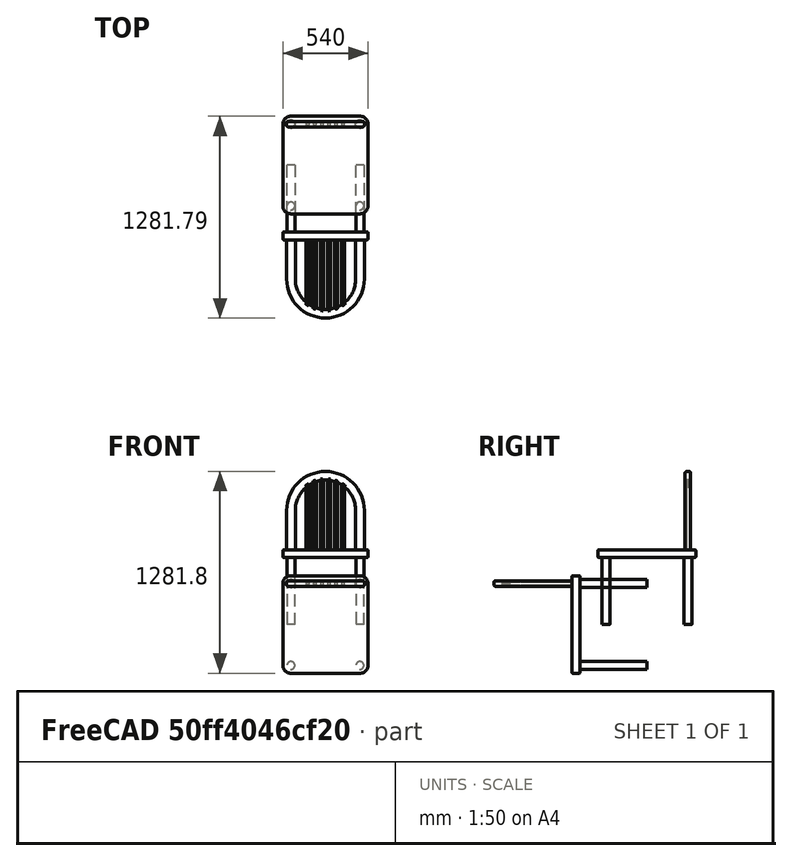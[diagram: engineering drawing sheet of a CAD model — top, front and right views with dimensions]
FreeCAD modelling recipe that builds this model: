
FCSTD DOCUMENT  (FreeCAD 1.0R39109 (Git))
Label: chair01
License: All rights reserved
LicenseURL: https://en.wikipedia.org/wiki/All_rights_reserved
objects: TechDraw::DrawViewDimension×38, Sketcher::SketchObject×8, PartDesign::Pad×8, TechDraw::DrawViewBalloon×7, TechDraw::DrawViewAnnotation×7, PartDesign::Body×6, TechDraw::DrawProjGroupItem×6, TechDraw::DrawSVGTemplate×5, TechDraw::DrawPage×5, PartDesign::SubShapeBinder×4, App::Part×3, PartDesign::Fillet×3, TechDraw::DrawViewSection×2, TechDraw::DrawViewDetail×1, TechDraw::DrawProjGroup×1, Part::FeaturePython×1
note: 130 computed .brp shape members not serialized (recipe doc carries the construction recipe); baked Part::Feature solids carry a one-line shape summary decoded from their .brp

FEATURE [Sketcher::SketchObject] Sketch
  ArcFitTolerance = 1e-06
  AttachmentSupport = -> [XZ_Plane]
  FullyConstrained = true
  MakeInternals = false
  MapMode = 5
  Placement = pos=(0,0,0) rot=(1,0,0;1.5708rad)
  sketch-geometry (6):
    g0: LineSegment [constr] StartX=-219 StartY=-260 StartZ=0 EndX=219 EndY=-260 EndZ=0
    g1: LineSegment [constr] StartX=219 StartY=-260 StartZ=0 EndX=219 EndY=260 EndZ=0
    g2: LineSegment [constr] StartX=219 StartY=260 StartZ=0 EndX=-219 EndY=260 EndZ=0
    g3: LineSegment [constr] StartX=-219 StartY=260 StartZ=0 EndX=-219 EndY=-260 EndZ=0
    g4: GeomPoint [constr] X=0 Y=0 Z=0
    g5: Circle CenterX=219 CenterY=-260 CenterZ=0 NormalX=0 NormalY=0 NormalZ=1 AngleXU=0 Radius=25
  constraints (14):
    c: Coincident(g0,g1)
    c: Coincident(g1,g2)
    c: Coincident(g2,g3)
    c: Coincident(g3,g0)
    c: Horizontal(g0)
    c: Horizontal(g2)
    c: Vertical(g1)
    c: Vertical(g3)
    c: Symmetric(g2,g0,g4)
    c: Distance(g1,g3) = 438
    c: Distance(g0,g2) = 520
    c: Coincident(g4,g-1)
    c: Diameter(g5) = 50
    c: Coincident(g5,g0)
FEATURE [PartDesign::Pad] Pad
  Direction = (0,-1,2e-16)
  Length = 425
  Length2 = 10
  Placement = pos=(0,0,0) rot=(1,0,0;1.5708rad)
  Profile = -> Sketch
  ReferenceAxis = -> Sketch [N_Axis]
  Refine = true
  Suppressed = false
  Type = 0
FEATURE [PartDesign::Body] Body  label="foot1"
  AllowCompound = false
  Group = -> [Sketch,Pad]
  Origin = -> Origin
  Tip = -> Pad
FEATURE [PartDesign::SubShapeBinder] Binder
  BindCopyOnChange = 0
  BindMode = 0
  ClaimChildren = false
  Context = -> Part001 [Body001.Binder.]
  Fuse = false
  MakeFace = true
  OffsetFill = false
  OffsetIntersection = false
  OffsetJoinType = 0
  OffsetOpenResult = false
  PartialLoad = false
  Refine = true
  Relative = true
  Support = -> [Pad[Face3]]
  _Version = 2
FEATURE [Sketcher::SketchObject] Sketch001
  ArcFitTolerance = 1e-06
  AttachmentSupport = -> [Binder]
  ExternalGeometry = -> [Binder]
  FullyConstrained = true
  MakeInternals = false
  MapMode = 5
  Placement = pos=(0,-425,0) rot=(1,0,0;1.5708rad)
  sketch-geometry (5):
    g0: LineSegment StartX=-270 StartY=310 StartZ=0 EndX=-270 EndY=-310 EndZ=0
    g1: LineSegment StartX=-270 StartY=-310 StartZ=0 EndX=270 EndY=-310 EndZ=0
    g2: LineSegment StartX=270 StartY=-310 StartZ=0 EndX=270 EndY=310 EndZ=0
    g3: LineSegment StartX=270 StartY=310 StartZ=0 EndX=-270 EndY=310 EndZ=0
    g4: GeomPoint [constr] X=0 Y=0 Z=0
  constraints (12):
    c: Coincident(g0,g1)
    c: Coincident(g1,g2)
    c: Coincident(g2,g3)
    c: Coincident(g3,g0)
    c: Vertical(g0)
    c: Vertical(g2)
    c: Horizontal(g1)
    c: Horizontal(g3)
    c: Symmetric(g2,g0,g4)
    c: Coincident(g4,g-1)
    c: DistanceX(g1,g1) = 540
    c: DistanceY(g2,g2) = 620
FEATURE [PartDesign::Pad] Pad001
  Direction = (0,-1,2e-16)
  Length = 50
  Length2 = 10
  Profile = -> Sketch001
  ReferenceAxis = -> Sketch001 [N_Axis]
  Refine = true
  Suppressed = false
  Type = 0
FEATURE [Sketcher::SketchObject] Sketch002
  ArcFitTolerance = 1e-06
  AttachmentSupport = -> [XZ_Plane002]
  FullyConstrained = true
  MakeInternals = false
  MapMode = 5
  Placement = pos=(0,0,0) rot=(1,0,0;1.5708rad)
  sketch-geometry (6):
    g0: LineSegment [constr] StartX=-219 StartY=-260 StartZ=0 EndX=219 EndY=-260 EndZ=0
    g1: LineSegment [constr] StartX=219 StartY=-260 StartZ=0 EndX=219 EndY=260 EndZ=0
    g2: LineSegment [constr] StartX=219 StartY=260 StartZ=0 EndX=-219 EndY=260 EndZ=0
    g3: LineSegment [constr] StartX=-219 StartY=260 StartZ=0 EndX=-219 EndY=-260 EndZ=0
    g4: GeomPoint [constr] X=0 Y=0 Z=0
    g5: Circle CenterX=219 CenterY=260 CenterZ=0 NormalX=0 NormalY=0 NormalZ=1 AngleXU=0 Radius=25
  constraints (14):
    c: Coincident(g0,g1)
    c: Coincident(g1,g2)
    c: Coincident(g2,g3)
    c: Coincident(g3,g0)
    c: Horizontal(g0)
    c: Horizontal(g2)
    c: Vertical(g1)
    c: Vertical(g3)
    c: Symmetric(g2,g0,g4)
    c: Distance(g1,g3) = 438
    c: Distance(g0,g2) = 520
    c: Coincident(g4,g-1)
    c: Coincident(g5,g1)
    c: Diameter(g5) = 50
FEATURE [PartDesign::Pad] Pad002
  Direction = (0,-1,2e-16)
  Length = 425
  Length2 = 10
  Placement = pos=(0,0,0) rot=(1,0,0;1.5708rad)
  Profile = -> Sketch002
  ReferenceAxis = -> Sketch002 [N_Axis]
  Refine = true
  Suppressed = false
  Type = 0
FEATURE [PartDesign::Body] Body002  label="foot2"
  AllowCompound = false
  Group = -> [Sketch002,Pad002]
  Origin = -> Origin002
  Tip = -> Pad002
FEATURE [Sketcher::SketchObject] Sketch003
  ArcFitTolerance = 1e-06
  AttachmentSupport = -> [XZ_Plane003]
  FullyConstrained = true
  MakeInternals = false
  MapMode = 5
  Placement = pos=(0,0,0) rot=(1,0,0;1.5708rad)
  sketch-geometry (6):
    g0: LineSegment [constr] StartX=-219 StartY=-260 StartZ=0 EndX=219 EndY=-260 EndZ=0
    g1: LineSegment [constr] StartX=219 StartY=-260 StartZ=0 EndX=219 EndY=260 EndZ=0
    g2: LineSegment [constr] StartX=219 StartY=260 StartZ=0 EndX=-219 EndY=260 EndZ=0
    g3: LineSegment [constr] StartX=-219 StartY=260 StartZ=0 EndX=-219 EndY=-260 EndZ=0
    g4: GeomPoint [constr] X=0 Y=0 Z=0
    g5: Circle CenterX=-219 CenterY=-260 CenterZ=0 NormalX=0 NormalY=0 NormalZ=1 AngleXU=0 Radius=25
  constraints (14):
    c: Coincident(g0,g1)
    c: Coincident(g1,g2)
    c: Coincident(g2,g3)
    c: Coincident(g3,g0)
    c: Horizontal(g0)
    c: Horizontal(g2)
    c: Vertical(g1)
    c: Vertical(g3)
    c: Symmetric(g2,g0,g4)
    c: Distance(g1,g3) = 438
    c: Distance(g0,g2) = 520
    c: Coincident(g4,g-1)
    c: Coincident(g5,g0)
    c: Diameter(g5) = 50
FEATURE [PartDesign::Pad] Pad003
  Direction = (0,-1,2e-16)
  Length = 425
  Length2 = 10
  Placement = pos=(0,0,0) rot=(1,0,0;1.5708rad)
  Profile = -> Sketch003
  ReferenceAxis = -> Sketch003 [N_Axis]
  Refine = true
  Suppressed = false
  Type = 0
FEATURE [PartDesign::Body] Body003  label="foot3"
  AllowCompound = false
  Group = -> [Sketch003,Pad003]
  Origin = -> Origin003
  Tip = -> Pad003
FEATURE [Sketcher::SketchObject] Sketch004
  ArcFitTolerance = 1e-06
  AttachmentSupport = -> [XZ_Plane004]
  FullyConstrained = false
  MakeInternals = false
  MapMode = 5
  Placement = pos=(0,0,0) rot=(1,0,0;1.5708rad)
  sketch-geometry (6):
    g0: LineSegment [constr] StartX=-219 StartY=-260 StartZ=0 EndX=219 EndY=-260 EndZ=0
    g1: LineSegment [constr] StartX=-219 StartY=260 StartZ=0 EndX=-219 EndY=-260 EndZ=0
    g2: GeomPoint [constr] X=0 Y=0 Z=0
    g3: Circle CenterX=-219 CenterY=260 CenterZ=0 NormalX=0 NormalY=0 NormalZ=1 AngleXU=0 Radius=25
    g4: LineSegment [constr] StartX=219 StartY=260 StartZ=0 EndX=219 EndY=-260 EndZ=0
    g5: LineSegment [constr] StartX=-219 StartY=260 StartZ=0 EndX=219 EndY=260 EndZ=0
  constraints (12):
    c: Coincident(g1,g0)
    c: Horizontal(g0)
    c: Vertical(g1)
    c: Symmetric(g4,g0,g2)
    c: Distance(g0,g1) = 520
    c: Coincident(g2,g-1)
    c: Diameter(g3) = 50
    c: Coincident(g4,g0)
    c: Vertical(g4)
    c: Coincident(g5,g3)
    c: Coincident(g5,g4)
    c: Horizontal(g5)
FEATURE [PartDesign::Pad] Pad004
  Direction = (0,-1,2e-16)
  Length = 425
  Length2 = 10
  Placement = pos=(0,0,0) rot=(1,0,0;1.5708rad)
  Profile = -> Sketch004
  ReferenceAxis = -> Sketch004 [N_Axis]
  Refine = true
  Suppressed = false
  Type = 0
FEATURE [PartDesign::Body] Body004  label="foot4"
  AllowCompound = false
  Group = -> [Sketch004,Pad004]
  Origin = -> Origin004
  Tip = -> Pad004
FEATURE [App::Part] Part  label="foot"
  Group = -> [Body004,Body003,Body002,Body]
  Origin = -> Origin005
FEATURE [PartDesign::SubShapeBinder] Binder001
  BindCopyOnChange = 0
  BindMode = 0
  ClaimChildren = false
  Context = -> Part001 [Body005.Binder001.]
  Fuse = false
  MakeFace = true
  OffsetFill = false
  OffsetIntersection = false
  OffsetJoinType = 0
  OffsetOpenResult = false
  PartialLoad = false
  Refine = true
  Relative = true
  Support = -> [Body001]
  _Version = 2
FEATURE [PartDesign::SubShapeBinder] Binder002
  BindCopyOnChange = 0
  BindMode = 0
  ClaimChildren = false
  Context = -> Part001 [Body005.Binder002.]
  Fuse = false
  MakeFace = true
  OffsetFill = false
  OffsetIntersection = false
  OffsetJoinType = 0
  OffsetOpenResult = false
  PartialLoad = false
  Refine = true
  Relative = true
  Support = -> [Part[Body004.]]
  _Version = 2
FEATURE [Sketcher::SketchObject] Sketch005
  ArcFitTolerance = 1e-06
  AttachmentSupport = -> [Binder001]
  ExternalGeometry = -> [Binder002]
  FullyConstrained = true
  MakeInternals = false
  MapMode = 5
  Placement = pos=(0,-475,0) rot=(1,0,0;1.5708rad)
  sketch-geometry (5):
    g0: LineSegment StartX=-246.5 StartY=242.5 StartZ=0 EndX=-191.5 EndY=242.5 EndZ=0
    g1: LineSegment StartX=-191.5 StartY=242.5 StartZ=0 EndX=-191.5 EndY=277.5 EndZ=0
    g2: LineSegment StartX=-191.5 StartY=277.5 StartZ=0 EndX=-246.5 EndY=277.5 EndZ=0
    g3: LineSegment StartX=-246.5 StartY=277.5 StartZ=0 EndX=-246.5 EndY=242.5 EndZ=0
    g4: GeomPoint [constr] X=-219 Y=260 Z=0
  constraints (12):
    c: Coincident(g0,g1)
    c: Coincident(g1,g2)
    c: Coincident(g2,g3)
    c: Coincident(g3,g0)
    c: Horizontal(g0)
    c: Horizontal(g2)
    c: Vertical(g1)
    c: Vertical(g3)
    c: Symmetric(g2,g0,g4)
    c: Coincident(g4,g-3)
    c: DistanceX(g2,g2) = 55
    c: DistanceY(g1,g1) = 35
FEATURE [PartDesign::Pad] Pad005
  Direction = (0,-1,2e-16)
  Length = 250
  Length2 = 10
  Profile = -> Sketch005
  ReferenceAxis = -> Sketch005 [N_Axis]
  Refine = true
  Suppressed = false
  Type = 0
FEATURE [PartDesign::SubShapeBinder] Binder003
  BindCopyOnChange = 0
  BindMode = 0
  ClaimChildren = false
  Context = -> Part001 [Body005.Binder003.]
  Fuse = false
  MakeFace = true
  OffsetFill = false
  OffsetIntersection = false
  OffsetJoinType = 0
  OffsetOpenResult = false
  PartialLoad = false
  Refine = true
  Relative = true
  Support = -> [Part[Body002.]]
  _Version = 2
FEATURE [Sketcher::SketchObject] Sketch006
  ArcFitTolerance = 1e-06
  AttachmentSupport = -> [Pad005]
  ExternalGeometry = -> [Pad005,Binder003]
  FullyConstrained = true
  MakeInternals = false
  MapMode = 5
  Placement = pos=(0,5.34e-14,242.5) rot=(1,0,0;3.14159rad)
  sketch-geometry (6):
    g0: LineSegment StartX=192.09 StartY=475 StartZ=0 EndX=192.09 EndY=725 EndZ=0
    g1: LineSegment StartX=247.09 StartY=475 StartZ=0 EndX=247.09 EndY=725 EndZ=0
    g2: LineSegment StartX=192.09 StartY=475 StartZ=0 EndX=247.09 EndY=475 EndZ=0
    g3: ArcOfCircle CenterX=0.295 CenterY=725 CenterZ=0 NormalX=0 NormalY=0 NormalZ=1 AngleXU=0 Radius=191.795 StartAngle=0 EndAngle=3.14159
    g4: ArcOfCircle CenterX=0.295 CenterY=725 CenterZ=0 NormalX=0 NormalY=0 NormalZ=1 AngleXU=0 Radius=246.795 StartAngle=1e-16 EndAngle=3.14159
    g5: LineSegment StartX=-246.5 StartY=725 StartZ=0 EndX=-191.5 EndY=725 EndZ=0
  constraints (16):
    c: Parallel(g1,g0)
    c: Horizontal(g0,g1)
    c: Horizontal(g1,g-3)
    c: Vertical(g1)
    c: Horizontal(g2)
    c: Coincident(g1,g2)
    c: Coincident(g0,g2)
    c: Coincident(g3,g-3)
    c: Coincident(g4,g-3)
    c: Tangent(g4,g1) = -1.5708
    c: Equal(g2,g-5)
    c: DistanceX(g0) = 192.09
    c: Tangent(g3,g0) = -1.5708
    c: Equal(g-6,g0)
    c: Coincident(g5,g4)
    c: Coincident(g5,g3)
FEATURE [PartDesign::Pad] Pad006
  BaseFeature = -> Pad005
  Direction = (0,0,-1)
  Length = 35
  Length2 = 10
  Profile = -> Sketch006
  ReferenceAxis = -> Sketch006 [N_Axis]
  Refine = true
  Reversed = true
  Suppressed = false
  Type = 0
FEATURE [Sketcher::SketchObject] Sketch007
  ArcFitTolerance = 1e-06
  AttachmentSupport = -> [Binder001]
  ExternalGeometry = -> [Pad006]
  FullyConstrained = true
  MakeInternals = false
  MapMode = 5
  Placement = pos=(0,-475,0) rot=(1,0,0;1.5708rad)
  sketch-geometry (13):
    g0: Circle CenterX=-112.5 CenterY=260 CenterZ=0 NormalX=0 NormalY=0 NormalZ=1 AngleXU=0 Radius=10
    g1: Circle CenterX=-67.5 CenterY=260 CenterZ=0 NormalX=0 NormalY=0 NormalZ=1 AngleXU=0 Radius=10
    g2: Circle CenterX=-22.5 CenterY=260 CenterZ=0 NormalX=0 NormalY=0 NormalZ=1 AngleXU=0 Radius=10
    g3: Circle CenterX=22.5 CenterY=260 CenterZ=0 NormalX=0 NormalY=0 NormalZ=1 AngleXU=0 Radius=10
    g4: Circle CenterX=67.5 CenterY=260 CenterZ=0 NormalX=0 NormalY=0 NormalZ=1 AngleXU=0 Radius=10
    g5: Circle CenterX=112.5 CenterY=260 CenterZ=0 NormalX=0 NormalY=0 NormalZ=1 AngleXU=0 Radius=10
    g6: LineSegment [constr] StartX=-112.5 StartY=260 StartZ=0 EndX=-67.5 EndY=260 EndZ=0
    g7: LineSegment [constr] StartX=-67.5 StartY=260 StartZ=0 EndX=-22.5 EndY=260 EndZ=0
    g8: LineSegment [constr] StartX=-22.5 StartY=260 StartZ=0 EndX=22.5 EndY=260 EndZ=0
    g9: LineSegment [constr] StartX=22.5 StartY=260 StartZ=0 EndX=67.5 EndY=260 EndZ=0
    g10: LineSegment [constr] StartX=67.5 StartY=260 StartZ=0 EndX=112.5 EndY=260 EndZ=0
    g11: LineSegment [constr] StartX=-191.5 StartY=260 StartZ=0 EndX=-112.5 EndY=260 EndZ=0
    g12: LineSegment [constr] StartX=112.5 StartY=260 StartZ=0 EndX=192.09 EndY=260 EndZ=0
  constraints (31):
    c: Coincident(g6,g0)
    c: Coincident(g6,g1)
    c: Horizontal(g6)
    c: Coincident(g7,g1)
    c: Coincident(g7,g2)
    c: Coincident(g8,g2)
    c: Coincident(g8,g3)
    c: Coincident(g9,g3)
    c: Coincident(g9,g4)
    c: Coincident(g10,g4)
    c: Coincident(g10,g5)
    c: Horizontal(g10)
    c: Equal(g6,g7)
    c: Equal(g7,g8)
    c: Equal(g8,g9)
    c: Equal(g9,g10)
    c: Equal(g0,g1)
    c: Equal(g1,g2)
    c: Equal(g2,g3)
    c: Equal(g3,g4)
    c: Equal(g4,g5)
    c: Horizontal(g7)
    c: Horizontal(g9)
    c: Coincident(g11,g0)
    c: Horizontal(g11)
    c: Coincident(g12,g5)
    c: Symmetric(g-4,g-4,g12)
    c: Symmetric(g-3,g-3,g11)
    c: Symmetric(g3,g2,g-2)
    c: Diameter(g0) = 20
    c: DistanceX(g2,g3) = 45
FEATURE [PartDesign::Pad] Pad007
  BaseFeature = -> Pad006
  Direction = (0,-1,2e-16)
  Length = 445
  Length2 = 10
  Profile = -> Sketch007
  ReferenceAxis = -> Sketch007 [N_Axis]
  Refine = true
  Suppressed = false
  Type = 0
FEATURE [PartDesign::Fillet] Fillet
  Base = -> Pad007 [Edge13,Edge19,Edge15,Edge16]
  BaseFeature = -> Pad007
  Radius = 10
  Refine = true
  SupportTransform = false
  Suppressed = false
  UseAllEdges = false
FEATURE [PartDesign::Body] Body005  label="backrest"
  AllowCompound = false
  Group = -> [Binder001,Sketch005,Binder002,Pad005,Sketch006,Binder003,Pad006,Sketch007,Pad007,Fillet]
  Origin = -> Origin006
  Tip = -> Fillet
FEATURE [PartDesign::Fillet] Fillet001
  Base = -> Pad001 [Edge5,Edge2,Edge8,Edge1]
  BaseFeature = -> Pad001
  Radius = 50
  Refine = true
  SupportTransform = false
  Suppressed = false
  UseAllEdges = false
FEATURE [PartDesign::Fillet] Fillet002
  Base = -> Fillet001 [Edge20,Edge8]
  BaseFeature = -> Fillet001
  Radius = 5
  Refine = true
  SupportTransform = false
  Suppressed = false
  UseAllEdges = false
FEATURE [PartDesign::Body] Body001  label="seat_surface"
  AllowCompound = false
  Group = -> [Binder,Sketch001,Pad001,Fillet001,Fillet002]
  Origin = -> Origin001
  Tip = -> Fillet002
FEATURE [App::Part] Part001  label="chair01_p"
  Group = -> [Body001,Part,Body005]
  Origin = -> Origin007
FEATURE [TechDraw::DrawSVGTemplate] Template  label="テンプレート"
  Height = 210
  Orientation = 1
  Template = <userpath>/AppData/Local/Programs/FreeCAD 1.0/data/Mod/TechDraw/Templates/A4_Landscape_blank.svg
  Width = 297
FEATURE [TechDraw::DrawProjGroupItem] View  label="平面図"
  CoarseView = false
  Direction = (0,-1,0)
  Focus = 100
  HardHidden = true
  IsoCount = 0
  IsoHidden = false
  IsoVisible = false
  LockPosition = false
  Perspective = false
  Rotation = 0
  RotationVector = (1,0,0)
  Scale = 0.25
  ScaleType = 2
  ScrubCount = 1
  SeamHidden = false
  SeamVisible = false
  SmoothHidden = false
  SmoothVisible = true
  Source = -> [Part001]
  Type = 0
  X = 141.468
  XDirection = (1,0,0)
  Y = 99.3312
FEATURE [TechDraw::DrawViewDimension] Dimension  label="寸法"
  AngleOverride = false
  Arbitrary = false
  ArbitraryTolerances = false
  BoxCorners = (2) [(-67.5,-77.5,-1e-07),(67.5,77.5,1e-07)]
  EqualTolerance = true
  ExtensionAngle = 0
  FormatSpec = %.2w
  FormatSpecOverTolerance = %+.2w
  FormatSpecUnderTolerance = %+.2w
  Inverted = false
  LineAngle = 0
  LockPosition = false
  MeasureType = 1
  OverTolerance = 0
  References2D = -> [View]
  Rotation = 0
  Scale = 0.2
  ScaleType = 2
  TheoreticalExact = false
  Type = 2
  UnderTolerance = 0
  X = 93.6885
  Y = 0
FEATURE [TechDraw::DrawViewDimension] Dimension001  label="寸法001"
  AngleOverride = false
  Arbitrary = false
  ArbitraryTolerances = false
  BoxCorners = (2) [(-67.5,-77.5,-1e-07),(67.5,77.5,1e-07)]
  EqualTolerance = true
  ExtensionAngle = 0
  FormatSpec = %.2w
  FormatSpecOverTolerance = %+.2w
  FormatSpecUnderTolerance = %+.2w
  Inverted = false
  LineAngle = 0
  LockPosition = false
  MeasureType = 1
  OverTolerance = 0
  References2D = -> [View]
  Rotation = 0
  Scale = 0.2
  ScaleType = 2
  TheoreticalExact = false
  Type = 2
  UnderTolerance = 0
  X = 76.7116
  Y = 0
FEATURE [TechDraw::DrawViewDimension] Dimension003  label="寸法003"
  AngleOverride = false
  Arbitrary = false
  ArbitraryTolerances = false
  BoxCorners = (2) [(-67.5,-77.5,-1e-07),(67.5,77.5,1e-07)]
  EqualTolerance = true
  ExtensionAngle = 0
  FormatSpec = %.2w
  FormatSpecOverTolerance = %+.2w
  FormatSpecUnderTolerance = %+.2w
  Inverted = false
  LineAngle = 0
  LockPosition = false
  MeasureType = 1
  OverTolerance = 0
  References2D = -> [View]
  Rotation = 0
  Scale = 0.2
  ScaleType = 2
  TheoreticalExact = false
  Type = 1
  UnderTolerance = 0
  X = 0
  Y = 106.033
FEATURE [TechDraw::DrawViewBalloon] Balloon  label="吹き出し"
  BubbleShape = 1
  EndType = 0
  EndTypeScale = 1
  KinkLength = 5
  LockPosition = false
  OriginX = 255.355
  OriginY = 295.355
  Rotation = 0
  Scale = 0.2
  ScaleType = 2
  ShapeScale = 1
  SourceView = -> View
  Text = R50
  TextWrapLen = -1
  X = 443.839
  Y = 387.538
FEATURE [TechDraw::DrawSVGTemplate] Template001  label="テンプレート001"
  Height = 210
  Orientation = 1
  Template = <userpath>/AppData/Local/Programs/FreeCAD 1.0/data/Mod/TechDraw/Templates/A4_Landscape_blank.svg
  Width = 297
FEATURE [TechDraw::DrawProjGroupItem] View001  label="正面図"
  CoarseView = false
  Direction = (0,0,-1)
  Focus = 100
  HardHidden = true
  IsoCount = 0
  IsoHidden = false
  IsoVisible = false
  LockPosition = false
  Perspective = false
  Rotation = 0
  RotationVector = (1,0,0)
  Scale = 0.2
  ScaleType = 2
  ScrubCount = 1
  SeamHidden = false
  SeamVisible = false
  SmoothHidden = false
  SmoothVisible = true
  Source = -> [Part001]
  Type = 0
  X = 64.7665
  XDirection = (1,0,0)
  Y = 110.024
FEATURE [TechDraw::DrawViewDimension] Dimension004  label="寸法004"
  AngleOverride = false
  Arbitrary = false
  ArbitraryTolerances = false
  BoxCorners = (2) [(-54,-97.1795,-1e-07),(54,97.1795,1e-07)]
  EqualTolerance = true
  ExtensionAngle = 0
  FormatSpec = %.2w
  FormatSpecOverTolerance = %+.2w
  FormatSpecUnderTolerance = %+.2w
  Inverted = false
  LineAngle = 0
  LockPosition = false
  MeasureType = 1
  OverTolerance = 0
  References2D = -> [View001]
  Rotation = 0
  Scale = 0.2
  ScaleType = 2
  TheoreticalExact = false
  Type = 2
  UnderTolerance = 0
  X = 82.1171
  Y = -54.6795
FEATURE [TechDraw::DrawViewDetail] Detail  label="Detail 詳細①"
  AnchorPoint = (266.87,-34.91,0)
  BaseView = -> View001
  CoarseView = false
  Direction = (0,0,-1)
  Focus = 100
  HardHidden = true
  IsoCount = 0
  IsoHidden = false
  IsoVisible = false
  LockPosition = false
  Perspective = false
  Radius = 30
  Reference = 詳細①
  Rotation = 0
  Scale = 1.2
  ScaleType = 2
  ScrubCount = 1
  SeamHidden = false
  SeamVisible = false
  ShowHighlight = true
  ShowMatting = true
  SmoothHidden = false
  SmoothVisible = true
  Source = -> [Part001]
  X = 216.677
  XDirection = (1,0,0)
  Y = 98.1897
FEATURE [TechDraw::DrawViewDimension] Dimension005  label="寸法005"
  AngleOverride = false
  Arbitrary = false
  ArbitraryTolerances = false
  BoxCorners = (2) [(-54,-97.1795,-1e-07),(54,97.1795,1e-07)]
  EqualTolerance = true
  ExtensionAngle = 0
  FormatSpec = R%.2w
  FormatSpecOverTolerance = %+.2w
  FormatSpecUnderTolerance = %+.2w
  Inverted = false
  LineAngle = 0
  LockPosition = false
  MeasureType = 1
  OverTolerance = 0
  References2D = -> [View001]
  Rotation = 0
  Scale = 0.2
  ScaleType = 2
  TheoreticalExact = false
  Type = 4
  UnderTolerance = 0
  X = 58.3026
  Y = 84.7593
FEATURE [TechDraw::DrawViewDimension] Dimension006  label="寸法006"
  AngleOverride = false
  Arbitrary = false
  ArbitraryTolerances = false
  BoxCorners = (2) [(-54,-97.1795,-1e-07),(54,97.1795,1e-07)]
  EqualTolerance = true
  ExtensionAngle = 0
  FormatSpec = %.2w
  FormatSpecOverTolerance = %+.2w
  FormatSpecUnderTolerance = %+.2w
  Inverted = false
  LineAngle = 0
  LockPosition = false
  MeasureType = 1
  OverTolerance = 0
  References2D = -> [View001]
  Rotation = 0
  Scale = 0.2
  ScaleType = 2
  TheoreticalExact = false
  Type = 2
  UnderTolerance = 0
  X = 84.137
  Y = 22.8205
FEATURE [TechDraw::DrawViewBalloon] Balloon001  label="吹き出し001"
  BubbleShape = 1
  EndType = 0
  EndTypeScale = 1
  KinkLength = 5
  LockPosition = false
  OriginX = 1.73973
  OriginY = 22.4786
  Rotation = 0
  Scale = 0.2
  ScaleType = 2
  ShapeScale = 1
  SourceView = -> Detail
  Text = R5
  TextWrapLen = -1
  X = 24.0571
  Y = 26.1222
FEATURE [TechDraw::DrawViewBalloon] Balloon002  label="吹き出し002"
  BubbleShape = 1
  EndType = 0
  EndTypeScale = 1
  KinkLength = 5
  LockPosition = false
  OriginX = 1.6677
  OriginY = -24.5252
  Rotation = 0
  Scale = 0.2
  ScaleType = 2
  ShapeScale = 1
  SourceView = -> Detail
  Text = R5
  TextWrapLen = -1
  X = 25.0104
  Y = -33.4181
FEATURE [TechDraw::DrawViewDimension] Dimension007  label="寸法007"
  AngleOverride = false
  Arbitrary = false
  ArbitraryTolerances = false
  BoxCorners = (2) [(-36.36,-28.8124,-1e-07),(3.75859,31.1876,1e-07)]
  EqualTolerance = true
  ExtensionAngle = 0
  FormatSpec = %.2w
  FormatSpecOverTolerance = %+.2w
  FormatSpecUnderTolerance = %+.2w
  Inverted = false
  LineAngle = 0
  LockPosition = false
  MeasureType = 1
  OverTolerance = 0
  References2D = -> [Detail]
  Rotation = 0
  Scale = 0.2
  ScaleType = 2
  TheoreticalExact = false
  Type = 2
  UnderTolerance = 0
  X = 11.0343
  Y = -1.18759
FEATURE [TechDraw::DrawViewDimension] Dimension008  label="寸法008"
  AngleOverride = false
  Arbitrary = false
  ArbitraryTolerances = false
  BoxCorners = (2) [(-54,-97.1795,-1e-07),(54,97.1795,1e-07)]
  EqualTolerance = true
  ExtensionAngle = 0
  FormatSpec = %.2w
  FormatSpecOverTolerance = %+.2w
  FormatSpecUnderTolerance = %+.2w
  Inverted = false
  LineAngle = 0
  LockPosition = false
  MeasureType = 1
  OverTolerance = 0
  References2D = -> [View001]
  Rotation = 0
  Scale = 0.2
  ScaleType = 2
  TheoreticalExact = false
  Type = 1
  UnderTolerance = 0
  X = 0
  Y = -39.2219
FEATURE [TechDraw::DrawViewDimension] Dimension009  label="寸法009"
  AngleOverride = false
  Arbitrary = false
  ArbitraryTolerances = false
  BoxCorners = (2) [(-54,-97.1795,-1e-07),(54,97.1795,1e-07)]
  EqualTolerance = true
  ExtensionAngle = 0
  FormatSpec = %.2w
  FormatSpecOverTolerance = %+.2w
  FormatSpecUnderTolerance = %+.2w
  Inverted = false
  LineAngle = 0
  LockPosition = false
  MeasureType = 1
  OverTolerance = 0
  References2D = -> [View001]
  Rotation = 0
  Scale = 0.2
  ScaleType = 2
  TheoreticalExact = false
  Type = 1
  UnderTolerance = 0
  X = 43.8
  Y = -102.091
FEATURE [TechDraw::DrawSVGTemplate] Template002  label="テンプレート002"
  Height = 210
  Orientation = 1
  Template = <userpath>/AppData/Local/Programs/FreeCAD 1.0/data/Mod/TechDraw/Templates/A4_Landscape_blank.svg
  Width = 297
FEATURE [TechDraw::DrawProjGroupItem] View002
  CoarseView = false
  Direction = (0,0,-1)
  Focus = 100
  HardHidden = true
  IsoCount = 0
  IsoHidden = false
  IsoVisible = false
  LockPosition = false
  Perspective = false
  Rotation = 0
  RotationVector = (1,0,0)
  Scale = 0.2
  ScaleType = 2
  ScrubCount = 1
  SeamHidden = false
  SeamVisible = false
  SmoothHidden = false
  SmoothVisible = true
  Source = -> [Part001]
  Type = 0
  X = 71.4869
  XDirection = (1,0,0)
  Y = 108.277
FEATURE [TechDraw::DrawViewSection] SectionView  label="セクション  - "
  BaseView = -> View002
  CoarseView = false
  CutSurfaceDisplay = 2
  Direction = (1e-16,1,0)
  FileGeomPattern = <userpath>\AppData\Local\Programs\FreeCAD 1.0\data\Mod/TechDraw/PAT/FCPAT.pat
  FileHatchPattern = <userpath>\AppData\Local\Programs\FreeCAD 1.0\data\Mod/TechDraw/Patterns/simple.svg
  Focus = 100
  FuseBeforeCut = false
  HardHidden = true
  HatchOffset = (0,0,0)
  HatchRotation = 0
  HatchScale = 1
  IsoCount = 0
  IsoHidden = false
  IsoVisible = false
  LockPosition = false
  NameGeomPattern = Diamond
  Perspective = false
  Rotation = 0
  Scale = 0.2
  ScaleType = 2
  ScrubCount = 1
  SeamHidden = false
  SeamVisible = false
  SectionDirection = 4
  SectionLineStretch = 1
  SectionNormal = (1e-16,1,0)
  SectionOrigin = (0,-579.9,0)
  SmoothHidden = false
  SmoothVisible = true
  Source = -> [Part001]
  TrimAfterCut = false
  UsePreviousCut = false
  X = 220.723
  XDirection = (1,-1e-16,0)
  Y = 183.206
FEATURE [TechDraw::DrawViewSection] SectionView001  label="セクション001  - "
  BaseView = -> View002
  CoarseView = false
  CutSurfaceDisplay = 2
  Direction = (1e-16,-1,0)
  FileGeomPattern = <userpath>\AppData\Local\Programs\FreeCAD 1.0\data\Mod/TechDraw/PAT/FCPAT.pat
  FileHatchPattern = <userpath>\AppData\Local\Programs\FreeCAD 1.0\data\Mod/TechDraw/Patterns/simple.svg
  Focus = 100
  FuseBeforeCut = false
  HardHidden = true
  HatchOffset = (0,0,0)
  HatchRotation = 0
  HatchScale = 1
  IsoCount = 0
  IsoHidden = false
  IsoVisible = false
  LockPosition = false
  NameGeomPattern = Diamond
  Perspective = false
  Rotation = 0
  Scale = 0.2
  ScaleType = 2
  ScrubCount = 1
  SeamHidden = false
  SeamVisible = false
  SectionDirection = 4
  SectionLineStretch = 1
  SectionNormal = (1e-16,-1,0)
  SectionOrigin = (0,-308.9,0)
  SmoothHidden = false
  SmoothVisible = true
  Source = -> [Part001]
  TrimAfterCut = false
  UsePreviousCut = false
  X = 220
  XDirection = (1,1e-16,0)
  Y = 69.8732
FEATURE [TechDraw::DrawViewAnnotation] Annotation  label="注釈"
  Font = osifont
  LineSpace = 100
  LockPosition = false
  MaxWidth = -1
  Rotation = 0
  Scale = 0.2
  ScaleType = 2
  Text = B-B
  TextSize = 5
  TextStyle = 0
  X = 220.723
  Y = 129.7
FEATURE [TechDraw::DrawViewAnnotation] Annotation001  label="注釈001"
  Font = osifont
  LineSpace = 100
  LockPosition = false
  MaxWidth = -1
  Rotation = 0
  Scale = 0.2
  ScaleType = 2
  Text = A-A
  TextSize = 5
  TextStyle = 0
  X = 220.723
  Y = 203.432
FEATURE [TechDraw::DrawViewAnnotation] Annotation002  label="注釈002"
  Font = osifont
  LineSpace = 100
  LockPosition = false
  MaxWidth = -1
  Rotation = 0
  Scale = 0.2
  ScaleType = 2
  Text = A
  TextSize = 5
  TextStyle = 0
  X = 7.47918
  Y = 141.949
FEATURE [TechDraw::DrawViewAnnotation] Annotation003  label="注釈003"
  Font = osifont
  LineSpace = 100
  LockPosition = false
  MaxWidth = -1
  Rotation = 0
  Scale = 0.2
  ScaleType = 2
  Text = B
  TextSize = 5
  TextStyle = 0
  X = 7.47918
  Y = 58.1769
FEATURE [TechDraw::DrawViewDimension] Dimension010  label="寸法010"
  AngleOverride = false
  Arbitrary = false
  ArbitraryTolerances = false
  BoxCorners = (2) [(-48.8,-57,0),(48.8,57,0)]
  EqualTolerance = true
  ExtensionAngle = 0
  FormatSpec = %.2w
  FormatSpecOverTolerance = %+.2w
  FormatSpecUnderTolerance = %+.2w
  Inverted = false
  LineAngle = 0
  LockPosition = false
  MeasureType = 1
  OverTolerance = 0
  References2D = -> [SectionView001]
  Rotation = 0
  Scale = 0.2
  ScaleType = 2
  TheoreticalExact = false
  Type = 1
  UnderTolerance = 0
  X = 0
  Y = 36.5611
FEATURE [TechDraw::DrawViewDimension] Dimension011  label="寸法011"
  AngleOverride = false
  Arbitrary = false
  ArbitraryTolerances = false
  BoxCorners = (2) [(-48.8,-57,0),(48.8,57,0)]
  EqualTolerance = true
  ExtensionAngle = 0
  FormatSpec = %.2w
  FormatSpecOverTolerance = %+.2w
  FormatSpecUnderTolerance = %+.2w
  Inverted = false
  LineAngle = 0
  LockPosition = false
  MeasureType = 1
  OverTolerance = 0
  References2D = -> [SectionView001]
  Rotation = 0
  Scale = 0.2
  ScaleType = 2
  TheoreticalExact = false
  Type = 2
  UnderTolerance = 0
  X = 57.2771
  Y = 0
FEATURE [TechDraw::DrawViewDimension] Dimension012  label="寸法012"
  AngleOverride = false
  Arbitrary = false
  ArbitraryTolerances = false
  BoxCorners = (2) [(-48.8,-57,0),(48.8,57,0)]
  EqualTolerance = true
  ExtensionAngle = 0
  FormatSpec = ⌀%.2w
  FormatSpecOverTolerance = %+.2w
  FormatSpecUnderTolerance = %+.2w
  Inverted = false
  LineAngle = 0
  LockPosition = false
  MeasureType = 1
  OverTolerance = 0
  References2D = -> [SectionView001]
  Rotation = 0
  Scale = 0.2
  ScaleType = 2
  TheoreticalExact = false
  Type = 5
  UnderTolerance = 0
  X = 29.2482
  Y = -33.2627
FEATURE [TechDraw::DrawViewDimension] Dimension013  label="寸法013"
  AngleOverride = false
  Arbitrary = false
  ArbitraryTolerances = false
  BoxCorners = (2) [(-49.359,-3.5,-1e-07),(49.359,3.5,1e-07)]
  EqualTolerance = true
  ExtensionAngle = 0
  FormatSpec = %.2w
  FormatSpecOverTolerance = %+.2w
  FormatSpecUnderTolerance = %+.2w
  Inverted = false
  LineAngle = 0
  LockPosition = false
  MeasureType = 1
  OverTolerance = 0
  References2D = -> [SectionView]
  Rotation = 0
  Scale = 0.2
  ScaleType = 2
  TheoreticalExact = false
  Type = 2
  UnderTolerance = 0
  X = 60.6113
  Y = 0
FEATURE [TechDraw::DrawViewDimension] Dimension014  label="寸法014"
  AngleOverride = false
  Arbitrary = false
  ArbitraryTolerances = false
  BoxCorners = (2) [(-49.359,-3.5,-1e-07),(49.359,3.5,1e-07)]
  EqualTolerance = true
  ExtensionAngle = 0
  FormatSpec = %.2w
  FormatSpecOverTolerance = %+.2w
  FormatSpecUnderTolerance = %+.2w
  Inverted = false
  LineAngle = 0
  LockPosition = false
  MeasureType = 1
  OverTolerance = 0
  References2D = -> [SectionView]
  Rotation = 0
  Scale = 0.2
  ScaleType = 2
  TheoreticalExact = false
  Type = 1
  UnderTolerance = 0
  X = 43.859
  Y = -19.0513
FEATURE [TechDraw::DrawViewDimension] Dimension015  label="寸法015"
  AngleOverride = false
  Arbitrary = false
  ArbitraryTolerances = false
  BoxCorners = (2) [(-49.359,-3.5,-1e-07),(49.359,3.5,1e-07)]
  EqualTolerance = true
  ExtensionAngle = 0
  FormatSpec = %.2w
  FormatSpecOverTolerance = %+.2w
  FormatSpecUnderTolerance = %+.2w
  Inverted = false
  LineAngle = 0
  LockPosition = false
  MeasureType = 1
  OverTolerance = 0
  References2D = -> [SectionView]
  Rotation = 0
  Scale = 0.2
  ScaleType = 2
  TheoreticalExact = false
  Type = 1
  UnderTolerance = 0
  X = -43.859
  Y = -19.0513
FEATURE [TechDraw::DrawViewDimension] Dimension016  label="寸法016"
  AngleOverride = false
  Arbitrary = false
  ArbitraryTolerances = false
  BoxCorners = (2) [(-49.359,-3.5,-1e-07),(49.359,3.5,1e-07)]
  EqualTolerance = true
  ExtensionAngle = 0
  FormatSpec = %.2w
  FormatSpecOverTolerance = %+.2w
  FormatSpecUnderTolerance = %+.2w
  Inverted = false
  LineAngle = 0
  LockPosition = false
  MeasureType = 1
  OverTolerance = 0
  References2D = -> [SectionView]
  Rotation = 0
  Scale = 0.2
  ScaleType = 2
  TheoreticalExact = false
  Type = 1
  UnderTolerance = 0
  X = 0
  Y = -26.0513
FEATURE [TechDraw::DrawViewDimension] Dimension017  label="寸法017"
  AngleOverride = false
  Arbitrary = false
  ArbitraryTolerances = false
  BoxCorners = (2) [(-67.5,-77.5,-1e-07),(67.5,77.5,1e-07)]
  EqualTolerance = true
  ExtensionAngle = 0
  FormatSpec = ⌀%.2w
  FormatSpecOverTolerance = %+.2w
  FormatSpecUnderTolerance = %+.2w
  Inverted = false
  LineAngle = 0
  LockPosition = false
  MeasureType = 1
  OverTolerance = 0
  References2D = -> [View]
  Rotation = 0
  Scale = 0.2
  ScaleType = 2
  TheoreticalExact = false
  Type = 5
  UnderTolerance = 0
  X = -43.531
  Y = -49.0379
FEATURE [TechDraw::DrawViewAnnotation] Annotation004  label="注釈004"
  Font = osifont
  LineSpace = 100
  LockPosition = false
  MaxWidth = -1
  Rotation = 0
  Scale = 0.2
  ScaleType = 2
  Text = A
  TextSize = 5
  TextStyle = 0
  X = 136.441
  Y = 143.535
FEATURE [TechDraw::DrawViewAnnotation] Annotation005  label="注釈005"
  Font = osifont
  LineSpace = 100
  LockPosition = false
  MaxWidth = -1
  Rotation = 0
  Scale = 0.2
  ScaleType = 2
  Text = B
  TextSize = 5
  TextStyle = 0
  X = 136.441
  Y = 58.1769
FEATURE [TechDraw::DrawViewAnnotation] Annotation006  label="注釈006"
  Font = osifont
  LineSpace = 100
  LockPosition = false
  MaxWidth = -1
  Rotation = 0
  Scale = 0.2
  ScaleType = 2
  Text = 詳細①
  TextSize = 5
  TextStyle = 0
  X = 216.677
  Y = 142.017
FEATURE [TechDraw::DrawPage] Page001  label="用紙001"
  KeepUpdated = true
  NextBalloonIndex = 5
  ProjectionType = 0
  Template = -> Template001
  Views = -> [View001,Dimension004,Detail,Dimension005,Dimension006,Balloon001,Balloon002,Dimension007,Dimension008,Dimension009,Annotation006]
FEATURE [TechDraw::DrawSVGTemplate] Template003  label="テンプレート003"
  Height = 210
  Orientation = 1
  Template = <userpath>/AppData/Local/Programs/FreeCAD 1.0/data/Mod/TechDraw/Templates/A4_Landscape_blank.svg
  Width = 297
FEATURE [TechDraw::DrawProjGroupItem] View003
  CoarseView = false
  Direction = (-1,0,-1e-16)
  Focus = 100
  HardHidden = true
  IsoCount = 0
  IsoHidden = false
  IsoVisible = false
  LockPosition = false
  Perspective = false
  Rotation = 0
  RotationVector = (1,0,0)
  Scale = 0.2
  ScaleType = 2
  ScrubCount = 1
  SeamHidden = false
  SeamVisible = false
  SmoothHidden = false
  SmoothVisible = true
  Source = -> [Part001]
  Type = 0
  X = 144.567
  XDirection = (1e-16,0,-1)
  Y = 103.689
FEATURE [TechDraw::DrawViewDimension] Dimension018  label="寸法018"
  AngleOverride = false
  Arbitrary = false
  ArbitraryTolerances = false
  BoxCorners = (2) [(-62,-97.1795,-1e-07),(62,97.1795,1e-07)]
  EqualTolerance = true
  ExtensionAngle = 0
  FormatSpec = %.2w
  FormatSpecOverTolerance = %+.2w
  FormatSpecUnderTolerance = %+.2w
  Inverted = false
  LineAngle = 0
  LockPosition = false
  MeasureType = 1
  OverTolerance = 0
  References2D = -> [View003]
  Rotation = 0
  Scale = 0.2
  ScaleType = 2
  TheoreticalExact = false
  Type = 1
  UnderTolerance = 0
  X = -52
  Y = 103.277
FEATURE [TechDraw::DrawViewDimension] Dimension019  label="寸法019"
  AngleOverride = false
  Arbitrary = false
  ArbitraryTolerances = false
  BoxCorners = (2) [(-62,-97.1795,-1e-07),(62,97.1795,1e-07)]
  EqualTolerance = true
  ExtensionAngle = 0
  FormatSpec = %.2w
  FormatSpecOverTolerance = %+.2w
  FormatSpecUnderTolerance = %+.2w
  Inverted = false
  LineAngle = 0
  LockPosition = false
  MeasureType = 1
  OverTolerance = 0
  References2D = -> [View003]
  Rotation = 0
  Scale = 0.2
  ScaleType = 2
  TheoreticalExact = false
  Type = 1
  UnderTolerance = 0
  X = 0
  Y = 21.4634
FEATURE [TechDraw::DrawViewDimension] Dimension021  label="寸法021"
  AngleOverride = false
  Arbitrary = false
  ArbitraryTolerances = false
  BoxCorners = (2) [(-62,-97.1795,-1e-07),(62,97.1795,1e-07)]
  EqualTolerance = true
  ExtensionAngle = 0
  FormatSpec = %.2w
  FormatSpecOverTolerance = %+.2w
  FormatSpecUnderTolerance = %+.2w
  Inverted = false
  LineAngle = 0
  LockPosition = false
  MeasureType = 1
  OverTolerance = 0
  References2D = -> [View003]
  Rotation = 0
  Scale = 0.2
  ScaleType = 2
  TheoreticalExact = false
  Type = 2
  UnderTolerance = 0
  X = -81.6899
  Y = 22.8205
FEATURE [TechDraw::DrawViewDimension] Dimension022  label="寸法022"
  AngleOverride = false
  Arbitrary = false
  ArbitraryTolerances = false
  BoxCorners = (2) [(-62,-97.1795,-1e-07),(62,97.1795,1e-07)]
  EqualTolerance = true
  ExtensionAngle = 0
  FormatSpec = %.2w
  FormatSpecOverTolerance = %+.2w
  FormatSpecUnderTolerance = %+.2w
  Inverted = false
  LineAngle = 0
  LockPosition = false
  MeasureType = 1
  OverTolerance = 0
  References2D = -> [View003]
  Rotation = 0
  Scale = 0.2
  ScaleType = 2
  TheoreticalExact = false
  Type = 2
  UnderTolerance = 0
  X = -81.6899
  Y = -7.1795
FEATURE [TechDraw::DrawViewDimension] Dimension023  label="寸法023"
  AngleOverride = false
  Arbitrary = false
  ArbitraryTolerances = false
  BoxCorners = (2) [(-62,-97.1795,-1e-07),(62,97.1795,1e-07)]
  EqualTolerance = true
  ExtensionAngle = 0
  FormatSpec = %.2w
  FormatSpecOverTolerance = %+.2w
  FormatSpecUnderTolerance = %+.2w
  Inverted = false
  LineAngle = 0
  LockPosition = false
  MeasureType = 1
  OverTolerance = 0
  References2D = -> [View003]
  Rotation = 0
  Scale = 0.2
  ScaleType = 2
  TheoreticalExact = false
  Type = 2
  UnderTolerance = 0
  X = -81.6899
  Y = -54.6795
FEATURE [TechDraw::DrawViewDimension] Dimension024  label="寸法024"
  AngleOverride = false
  Arbitrary = false
  ArbitraryTolerances = false
  BoxCorners = (2) [(-67.5,-77.5,-1e-07),(67.5,77.5,1e-07)]
  EqualTolerance = true
  ExtensionAngle = 0
  FormatSpec = %.2w
  FormatSpecOverTolerance = %+.2w
  FormatSpecUnderTolerance = %+.2w
  Inverted = false
  LineAngle = 0
  LockPosition = false
  MeasureType = 1
  OverTolerance = 0
  References2D = -> [View]
  Rotation = 0
  Scale = 0.2
  ScaleType = 2
  TheoreticalExact = false
  Type = 1
  UnderTolerance = 0
  X = -22.5
  Y = 86.1012
FEATURE [TechDraw::DrawViewDimension] Dimension027  label="寸法027"
  AngleOverride = false
  Arbitrary = false
  ArbitraryTolerances = false
  BoxCorners = (2) [(-67.5,-77.5,-1e-07),(67.5,77.5,1e-07)]
  EqualTolerance = true
  ExtensionAngle = 0
  FormatSpec = %.2w
  FormatSpecOverTolerance = %+.2w
  FormatSpecUnderTolerance = %+.2w
  Inverted = false
  LineAngle = 0
  LockPosition = false
  MeasureType = 1
  OverTolerance = 0
  References2D = -> [View]
  Rotation = 0
  Scale = 0.2
  ScaleType = 2
  TheoreticalExact = false
  Type = 1
  UnderTolerance = 0
  X = -11.25
  Y = 86.1012
FEATURE [TechDraw::DrawViewDimension] Dimension028  label="寸法028"
  AngleOverride = false
  Arbitrary = false
  ArbitraryTolerances = false
  BoxCorners = (2) [(-67.5,-77.5,-1e-07),(67.5,77.5,1e-07)]
  EqualTolerance = true
  ExtensionAngle = 0
  FormatSpec = %.2w
  FormatSpecOverTolerance = %+.2w
  FormatSpecUnderTolerance = %+.2w
  Inverted = false
  LineAngle = 0
  LockPosition = false
  MeasureType = 1
  OverTolerance = 0
  References2D = -> [View]
  Rotation = 0
  Scale = 0.2
  ScaleType = 2
  TheoreticalExact = false
  Type = 1
  UnderTolerance = 0
  X = 0
  Y = 86.1012
FEATURE [TechDraw::DrawViewDimension] Dimension029  label="寸法029"
  AngleOverride = false
  Arbitrary = false
  ArbitraryTolerances = false
  BoxCorners = (2) [(-67.5,-77.5,-1e-07),(67.5,77.5,1e-07)]
  EqualTolerance = true
  ExtensionAngle = 0
  FormatSpec = %.2w
  FormatSpecOverTolerance = %+.2w
  FormatSpecUnderTolerance = %+.2w
  Inverted = false
  LineAngle = 0
  LockPosition = false
  MeasureType = 1
  OverTolerance = 0
  References2D = -> [View]
  Rotation = 0
  Scale = 0.2
  ScaleType = 2
  TheoreticalExact = false
  Type = 1
  UnderTolerance = 0
  X = 11.25
  Y = 86.1012
FEATURE [TechDraw::DrawViewBalloon] Balloon003  label="吹き出し003"
  BubbleShape = 1
  EndType = 0
  EndTypeScale = 1
  KinkLength = 5
  LockPosition = false
  OriginX = -243.866
  OriginY = 14.5711
  Rotation = 0
  Scale = 0.2
  ScaleType = 2
  ShapeScale = 1
  SourceView = -> SectionView
  Text = R50
  TextWrapLen = -1
  X = -330.551
  Y = 60.4095
FEATURE [TechDraw::DrawViewDimension] Dimension031  label="寸法031"
  AngleOverride = false
  Arbitrary = false
  ArbitraryTolerances = false
  BoxCorners = (2) [(-49.359,-3.5,-1e-07),(49.359,3.5,1e-07)]
  EqualTolerance = true
  ExtensionAngle = 0
  FormatSpec = %.2w
  FormatSpecOverTolerance = %+.2w
  FormatSpecUnderTolerance = %+.2w
  Inverted = false
  LineAngle = 0
  LockPosition = false
  MeasureType = 1
  OverTolerance = 0
  References2D = -> [SectionView]
  Rotation = 0
  Scale = 0.2
  ScaleType = 2
  TheoreticalExact = false
  Type = 1
  UnderTolerance = 0
  X = -18.059
  Y = -10.5018
FEATURE [TechDraw::DrawViewDimension] Dimension032  label="寸法032"
  AngleOverride = false
  Arbitrary = false
  ArbitraryTolerances = false
  BoxCorners = (2) [(-49.359,-3.5,-1e-07),(49.359,3.5,1e-07)]
  EqualTolerance = true
  ExtensionAngle = 0
  FormatSpec = %.2w
  FormatSpecOverTolerance = %+.2w
  FormatSpecUnderTolerance = %+.2w
  Inverted = false
  LineAngle = 0
  LockPosition = false
  MeasureType = 1
  OverTolerance = 0
  References2D = -> [SectionView]
  Rotation = 0
  Scale = 0.2
  ScaleType = 2
  TheoreticalExact = false
  Type = 1
  UnderTolerance = 0
  X = -9.059
  Y = -10.5018
FEATURE [TechDraw::DrawViewDimension] Dimension033  label="寸法033"
  AngleOverride = false
  Arbitrary = false
  ArbitraryTolerances = false
  BoxCorners = (2) [(-49.359,-3.5,-1e-07),(49.359,3.5,1e-07)]
  EqualTolerance = true
  ExtensionAngle = 0
  FormatSpec = %.2w
  FormatSpecOverTolerance = %+.2w
  FormatSpecUnderTolerance = %+.2w
  Inverted = false
  LineAngle = 0
  LockPosition = false
  MeasureType = 1
  OverTolerance = 0
  References2D = -> [SectionView]
  Rotation = 0
  Scale = 0.2
  ScaleType = 2
  TheoreticalExact = false
  Type = 1
  UnderTolerance = 0
  X = -0.059
  Y = -10.5018
FEATURE [TechDraw::DrawViewDimension] Dimension034  label="寸法034"
  AngleOverride = false
  Arbitrary = false
  ArbitraryTolerances = false
  BoxCorners = (2) [(-49.359,-3.5,-1e-07),(49.359,3.5,1e-07)]
  EqualTolerance = true
  ExtensionAngle = 0
  FormatSpec = %.2w
  FormatSpecOverTolerance = %+.2w
  FormatSpecUnderTolerance = %+.2w
  Inverted = false
  LineAngle = 0
  LockPosition = false
  MeasureType = 1
  OverTolerance = 0
  References2D = -> [SectionView]
  Rotation = 0
  Scale = 0.2
  ScaleType = 2
  TheoreticalExact = false
  Type = 1
  UnderTolerance = 0
  X = 8.941
  Y = -10.5018
FEATURE [TechDraw::DrawViewDimension] Dimension035  label="寸法035"
  AngleOverride = false
  Arbitrary = false
  ArbitraryTolerances = false
  BoxCorners = (2) [(-49.359,-3.5,-1e-07),(49.359,3.5,1e-07)]
  EqualTolerance = true
  ExtensionAngle = 0
  FormatSpec = %.2w
  FormatSpecOverTolerance = %+.2w
  FormatSpecUnderTolerance = %+.2w
  Inverted = false
  LineAngle = 0
  LockPosition = false
  MeasureType = 1
  OverTolerance = 0
  References2D = -> [SectionView]
  Rotation = 0
  Scale = 0.2
  ScaleType = 2
  TheoreticalExact = false
  Type = 1
  UnderTolerance = 0
  X = 17.941
  Y = -10.5018
FEATURE [TechDraw::DrawViewDimension] Dimension036  label="寸法036"
  AngleOverride = false
  Arbitrary = false
  ArbitraryTolerances = false
  BoxCorners = (2) [(-48.8,-57,0),(48.8,57,0)]
  EqualTolerance = true
  ExtensionAngle = 0
  FormatSpec = ⌀%.2w
  FormatSpecOverTolerance = %+.2w
  FormatSpecUnderTolerance = %+.2w
  Inverted = false
  LineAngle = 0
  LockPosition = false
  MeasureType = 1
  OverTolerance = 0
  References2D = -> [SectionView001]
  Rotation = 0
  Scale = 0.2
  ScaleType = 2
  TheoreticalExact = false
  Type = 5
  UnderTolerance = 0
  X = -31.9928
  Y = -33.9465
FEATURE [TechDraw::DrawViewDimension] Dimension037  label="寸法037"
  AngleOverride = false
  Arbitrary = false
  ArbitraryTolerances = false
  BoxCorners = (2) [(-49.359,-3.5,-1e-07),(49.359,3.5,1e-07)]
  EqualTolerance = true
  ExtensionAngle = 0
  FormatSpec = R%.2w
  FormatSpecOverTolerance = %+.2w
  FormatSpecUnderTolerance = %+.2w
  Inverted = false
  LineAngle = 0
  LockPosition = false
  MeasureType = 1
  OverTolerance = 0
  References2D = -> [SectionView]
  Rotation = 0
  Scale = 0.2
  ScaleType = 2
  TheoreticalExact = false
  Type = 4
  UnderTolerance = 0
  X = -17.2572
  Y = 10.7644
FEATURE [TechDraw::DrawPage] Page002  label="用紙002"
  KeepUpdated = true
  NextBalloonIndex = 3
  ProjectionType = 0
  Template = -> Template002
  Views = -> [View002,SectionView,SectionView001,Annotation,Annotation001,Annotation002,Annotation003,Dimension010,Dimension011,Dimension012,Dimension013,Dimension014,Dimension015,Dimension016,Annotation004,Annotation005,Balloon003,Dimension031,Dimension032,Dimension033,Dimension034,Dimension035,Dimension036,Dimension037]
FEATURE [TechDraw::DrawViewDimension] Dimension038  label="寸法038"
  AngleOverride = false
  Arbitrary = false
  ArbitraryTolerances = false
  BoxCorners = (2) [(-67.5,-77.5,-1e-07),(67.5,77.5,1e-07)]
  EqualTolerance = true
  ExtensionAngle = 0
  FormatSpec = R%.2w
  FormatSpecOverTolerance = %+.2w
  FormatSpecUnderTolerance = %+.2w
  Inverted = false
  LineAngle = 0
  LockPosition = false
  MeasureType = 1
  OverTolerance = 0
  References2D = -> [View]
  Rotation = 0
  Scale = 0.2
  ScaleType = 2
  TheoreticalExact = false
  Type = 4
  UnderTolerance = 0
  X = -11.3998
  Y = 50.95
FEATURE [TechDraw::DrawViewBalloon] Balloon004  label="吹き出し004"
  BubbleShape = 1
  EndType = 0
  EndTypeScale = 1
  KinkLength = 5
  LockPosition = false
  OriginX = 308.536
  OriginY = -12.362
  Rotation = 0
  Scale = 0.2
  ScaleType = 2
  ShapeScale = 1
  SourceView = -> View003
  Text = R5
  TextWrapLen = -1
  X = 402.745
  Y = 52.3172
FEATURE [TechDraw::DrawViewBalloon] Balloon005  label="吹き出し005"
  BubbleShape = 1
  EndType = 0
  EndTypeScale = 1
  KinkLength = 5
  LockPosition = false
  OriginX = 308.536
  OriginY = -59.433
  Rotation = 0
  Scale = 0.2
  ScaleType = 2
  ShapeScale = 1
  SourceView = -> View003
  Text = R5
  TextWrapLen = -1
  X = 402.988
  Y = -126.489
FEATURE [TechDraw::DrawViewBalloon] Balloon006  label="吹き出し006"
  BubbleShape = 1
  EndType = 0
  EndTypeScale = 1
  KinkLength = 5
  LockPosition = false
  OriginX = -245.429
  OriginY = 482.969
  Rotation = 0
  Scale = 0.2
  ScaleType = 2
  ShapeScale = 1
  SourceView = -> View003
  Text = R10
  TextWrapLen = -1
  X = -110.739
  Y = 478.898
FEATURE [TechDraw::DrawPage] Page003  label="用紙003"
  KeepUpdated = true
  NextBalloonIndex = 7
  ProjectionType = 0
  Template = -> Template003
  Views = -> [View003,Dimension018,Dimension019,Dimension021,Dimension022,Dimension023,Balloon004,Balloon005,Balloon006]
FEATURE [TechDraw::DrawSVGTemplate] Template004  label="テンプレート004"
  Height = 210
  Orientation = 1
  Template = <userpath>/AppData/Local/Programs/FreeCAD 1.0/data/Mod/TechDraw/Templates/A4_Landscape_blank.svg
  Width = 297
FEATURE [TechDraw::DrawProjGroupItem] View004  label="Front"
  CoarseView = false
  Direction = (0,0,-1)
  Focus = 100
  HardHidden = true
  IsoCount = 0
  IsoHidden = false
  IsoVisible = false
  LockPosition = true
  Perspective = false
  Rotation = 0
  RotationVector = (1,0,0)
  Scale = 0.166667
  ScaleType = 2
  ScrubCount = 1
  SeamHidden = false
  SeamVisible = false
  SmoothHidden = false
  SmoothVisible = true
  Source = -> [Part001]
  Type = 0
  X = 0
  XDirection = (1,0,0)
  Y = 0
FEATURE [TechDraw::DrawProjGroupItem] ProjItem001  label="前面 右上"
  CoarseView = false
  Direction = (0.57735,-0.57735,-0.57735)
  Focus = 100
  HardHidden = true
  IsoCount = 0
  IsoHidden = false
  IsoVisible = false
  LockPosition = false
  Perspective = false
  Rotation = 0
  RotationVector = (1,0,0)
  Scale = 0.166667
  ScaleType = 2
  ScrubCount = 1
  SeamHidden = false
  SeamVisible = false
  SmoothHidden = false
  SmoothVisible = true
  Source = -> [Part001]
  Type = 7
  X = -124.902
  XDirection = (0.707107,0,0.707107)
  Y = -190.749
FEATURE [TechDraw::DrawProjGroup] ProjGroup
  Anchor = -> View004
  AutoDistribute = true
  LockPosition = false
  ProjectionType = 0
  Rotation = 0
  Scale = 0.166667
  ScaleType = 2
  Source = -> [Part001]
  Views = -> [View004,ProjItem001]
  X = 295.182
  Y = 339.692
  spacingX = 15
  spacingY = 15
FEATURE [TechDraw::DrawPage] Page004  label="用紙004"
  KeepUpdated = true
  NextBalloonIndex = 1
  ProjectionType = 0
  Template = -> Template004
  Views = -> [ProjGroup]
FEATURE [TechDraw::DrawViewDimension] Dimension039  label="寸法039"
  AngleOverride = false
  Arbitrary = false
  ArbitraryTolerances = false
  BoxCorners = (2) [(-67.5,-77.5,-1e-07),(67.5,77.5,1e-07)]
  EqualTolerance = true
  ExtensionAngle = 0
  FormatSpec = %.2w
  FormatSpecOverTolerance = %+.2w
  FormatSpecUnderTolerance = %+.2w
  Inverted = false
  LineAngle = 0
  LockPosition = false
  MeasureType = 1
  OverTolerance = 0
  References2D = -> [View]
  Rotation = 0
  Scale = 0.2
  ScaleType = 2
  TheoreticalExact = false
  Type = 0
  UnderTolerance = 0
  X = 22.5
  Y = 86.1012
FEATURE [TechDraw::DrawViewDimension] Dimension040  label="寸法040"
  AngleOverride = false
  Arbitrary = false
  ArbitraryTolerances = false
  BoxCorners = (2) [(-67.5,-77.5,-1e-07),(67.5,77.5,1e-07)]
  EqualTolerance = true
  ExtensionAngle = 0
  FormatSpec = %.2w
  FormatSpecOverTolerance = %+.2w
  FormatSpecUnderTolerance = %+.2w
  Inverted = false
  LineAngle = 0
  LockPosition = false
  MeasureType = 1
  OverTolerance = 0
  References2D = -> [View]
  Rotation = 0
  Scale = 0.2
  ScaleType = 2
  TheoreticalExact = false
  Type = 1
  UnderTolerance = 0
  X = 41.4375
  Y = 86.1012
FEATURE [TechDraw::DrawViewDimension] Dimension041  label="寸法041"
  AngleOverride = false
  Arbitrary = false
  ArbitraryTolerances = false
  BoxCorners = (2) [(-67.5,-77.5,-1e-07),(67.5,77.5,1e-07)]
  EqualTolerance = true
  ExtensionAngle = 0
  FormatSpec = %.2w
  FormatSpecOverTolerance = %+.2w
  FormatSpecUnderTolerance = %+.2w
  Inverted = false
  LineAngle = 0
  LockPosition = false
  MeasureType = 1
  OverTolerance = 0
  References2D = -> [View]
  Rotation = 0
  Scale = 0.2
  ScaleType = 2
  TheoreticalExact = false
  Type = 1
  UnderTolerance = 0
  X = -41.4375
  Y = 86.1012
FEATURE [TechDraw::DrawViewDimension] Dimension042  label="寸法042"
  AngleOverride = false
  Arbitrary = false
  ArbitraryTolerances = false
  BoxCorners = (2) [(-67.5,-77.5,-1e-07),(67.5,77.5,1e-07)]
  EqualTolerance = true
  ExtensionAngle = 0
  FormatSpec = %.2w
  FormatSpecOverTolerance = %+.2w
  FormatSpecUnderTolerance = %+.2w
  Inverted = false
  LineAngle = 0
  LockPosition = false
  MeasureType = 1
  OverTolerance = 0
  References2D = -> [View]
  Rotation = 0
  Scale = 0.2
  ScaleType = 2
  TheoreticalExact = false
  Type = 1
  UnderTolerance = 0
  X = 0
  Y = 96.0931
FEATURE [TechDraw::DrawPage] Page  label="用紙"
  KeepUpdated = true
  NextBalloonIndex = 5
  ProjectionType = 0
  Template = -> Template
  Views = -> [View,Dimension,Dimension001,Dimension003,Balloon,Dimension017,Dimension024,Dimension027,Dimension028,Dimension029,Dimension038,Dimension039,Dimension040,Dimension041,Dimension042]
FEATURE [Part::FeaturePython] Clone  label="chair01_clone"  # Draft clone (typed FeaturePython)
  AttacherType = Attacher::AttachEngine3D
  Fuse = false
  Objects = -> [Part001]
  Placement = pos=(0,0,0) rot=(1,0,0;-1.5708rad)
  Scale = (1,1,1)
FEATURE [App::Part] Part002  label="chair01"
  Group = -> [Clone]
  Origin = -> Origin008
